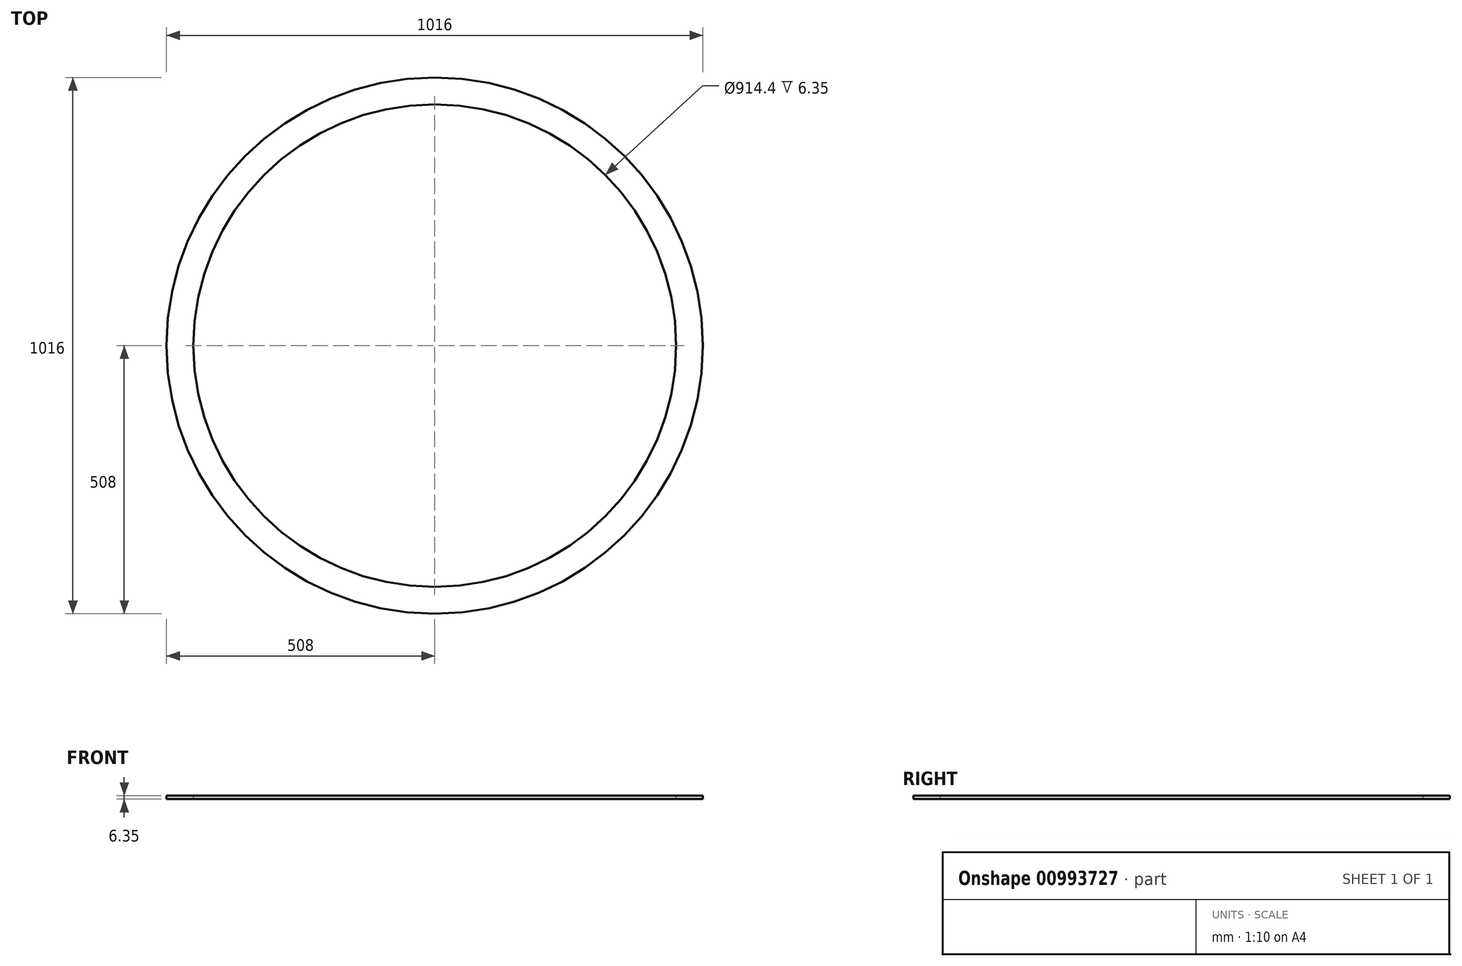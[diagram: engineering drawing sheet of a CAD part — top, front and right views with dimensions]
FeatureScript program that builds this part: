
annotation { "Feature Type Name" : "Feature", "Feature Type Description" : "" }
export const myFeature = defineFeature(function(context is Context, id is Id, definition is map)
    precondition{}
    {
        {
            var Q0;
            Q0=qCreatedBy(makeId("Top.planeOp"),FACE);
            var sketch = newSketch(context, id + "F0", { "sketchPlane" : qUnion([Q0])});
            skCircle(sketch, "E0", {"center": v(0, 0) * mm, "radius": 457.2 * mm});
            skCircle(sketch, "E1", {"center": v(0, 0) * mm, "radius": 508 * mm});
            skSolve(sketch);
        }
        {
            var Q0;
            Q0=makeQuery(id+"F0.imprint","IMPRINT",FACE,{"disambiguationData":[TD([[makeQuery(id+"F0.imprint","IMPRINT",EDGE,{"derivedFrom":sQuery(id+"F0.wireOp",EDGE,"E0")}),-1.0]])]});
            extrude(context, id + "F1", {"entities" : qUnion([Q0]), "depth" : 6.35 * mm, "offsetDistance" : 25.4 * mm});
        }
    });
